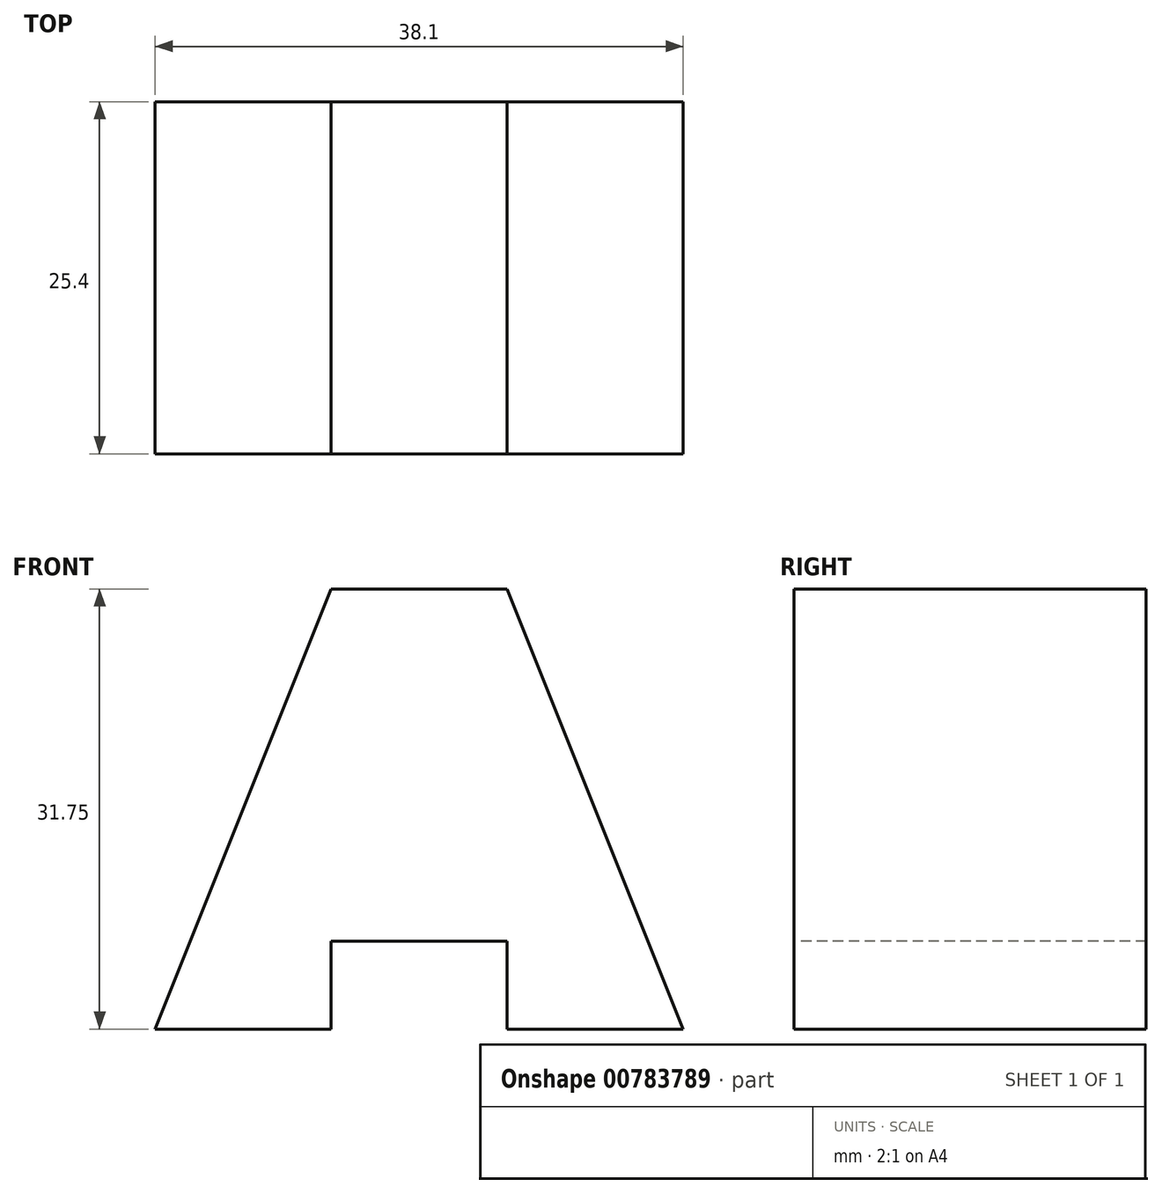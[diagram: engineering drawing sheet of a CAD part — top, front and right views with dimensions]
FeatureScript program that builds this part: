
annotation { "Feature Type Name" : "Feature", "Feature Type Description" : "" }
export const myFeature = defineFeature(function(context is Context, id is Id, definition is map)
    precondition{}
    {
        {
            var Q0;
            Q0=qCreatedBy(makeId("Front.planeOp"),FACE);
            var sketch = newSketch(context, id + "F0", { "sketchPlane" : qUnion([Q0])});
            skLineSegment(sketch, "E0", {"start": v(0, 0) * mm, "end": v(38.1, 0) * mm});
            skLineSegment(sketch, "E1", {"start": v(38.1, 0) * mm, "end": v(38.1, 31.75) * mm});
            skLineSegment(sketch, "E2", {"start": v(38.1, 31.75) * mm, "end": v(0, 31.75) * mm});
            skLineSegment(sketch, "E3", {"start": v(0, 31.75) * mm, "end": v(0, 0) * mm});
            skSolve(sketch);
        }
        {
            var Q0;
            Q0=makeQuery(id+"F0.imprint","IMPRINT",FACE,{"disambiguationData":[TD([[makeQuery(id+"F0.imprint","IMPRINT",EDGE,{"derivedFrom":sQuery(id+"F0.wireOp",EDGE,"E0")}),1.0]])]});
            extrude(context, id + "F1", {"entities" : qUnion([Q0]), "depth" : 25.4 * mm, "offsetDistance" : 25.4 * mm});
        }
        {
            var Q0;
            Q0=makeQuery(id+"F1.opExtrude","CAP_FACE",FACE,{"disambiguationData":[OSD([sQuery(id+"F0.wireOp",EDGE,"E0"),sQuery(id+"F0.wireOp",EDGE,"E1"),sQuery(id+"F0.wireOp",EDGE,"E2"),sQuery(id+"F0.wireOp",EDGE,"E3")])],"isStart":false});
            var sketch = newSketch(context, id + "F2", { "sketchPlane" : qUnion([Q0])});
            skLineSegment(sketch, "E4", {"start": v(0, 0) * mm, "end": v(12.7, 0) * mm});
            skLineSegment(sketch, "E5", {"start": v(12.7, 0) * mm, "end": v(12.7, 6.35) * mm});
            skLineSegment(sketch, "E6", {"start": v(12.7, 6.35) * mm, "end": v(25.4, 6.35) * mm});
            skLineSegment(sketch, "E7", {"start": v(25.4, 6.35) * mm, "end": v(25.4, 0) * mm});
            skLineSegment(sketch, "E8", {"start": v(25.4, 0) * mm, "end": v(38.1, 0) * mm});
            skSolve(sketch);
        }
        {
            var Q0;
            Q0 = qSketchRegion(id + "F2", true);
            var Q1;
            {var subQ0=sQuery(id+"F2.wireOp",EDGE,"E5");Q1=makeQuery(id+"F2.imprint","IMPRINT",FACE,{"disambiguationData":[TD([[makeQuery(id+"F2.imprint","IMPRINT",EDGE,{"derivedFrom":subQ0}),-1.0]])]});}
            extrude(context, id + "F3", {"entities" : qUnion([Q0, Q1]), "operationType" : NewBodyOperationType.REMOVE, "oppositeDirection" : true, "depth" : 25.4 * mm, "offsetDistance" : 25.4 * mm});
        }
        {
            var Q0;
            Q0=makeQuery(id+"F1.opExtrude","CAP_FACE",FACE,{"disambiguationData":[OSD([sQuery(id+"F0.wireOp",EDGE,"E0"),sQuery(id+"F0.wireOp",EDGE,"E1"),sQuery(id+"F0.wireOp",EDGE,"E2"),sQuery(id+"F0.wireOp",EDGE,"E3")])],"isStart":false});
            var sketch = newSketch(context, id + "F4", { "sketchPlane" : qUnion([Q0])});
            skLineSegment(sketch, "E9", {"start": v(0, 31.75) * mm, "end": v(12.7, 31.75) * mm});
            skLineSegment(sketch, "E10", {"start": v(12.7, 31.75) * mm, "end": v(25.4, 31.75) * mm});
            skLineSegment(sketch, "E11", {"start": v(25.4, 31.75) * mm, "end": v(38.1, 31.75) * mm});
            skLineSegment(sketch, "E12", {"start": v(0, 0) * mm, "end": v(12.7, 31.75) * mm});
            skLineSegment(sketch, "E13", {"start": v(25.4, 31.75) * mm, "end": v(38.1, 0) * mm});
            skSolve(sketch);
        }
        {
            var Q0;
            Q0 = qSketchRegion(id + "F4", true);
            var Q1;
            Q1=makeQuery(id+"F4.imprint","IMPRINT",FACE,{"disambiguationData":[TD([[makeQuery(id+"F4.imprint","IMPRINT",EDGE,{"derivedFrom":sQuery(id+"F4.wireOp",EDGE,"E9")}),1.0]])]});
            extrude(context, id + "F5", {"entities" : qUnion([Q0, Q1]), "operationType" : NewBodyOperationType.REMOVE, "oppositeDirection" : true, "depth" : 25.4 * mm, "offsetDistance" : 25.4 * mm});
        }
        {
            var Q0;
            Q0=makeQuery(id+"F1.opExtrude","CAP_FACE",FACE,{"disambiguationData":[OSD([sQuery(id+"F0.wireOp",EDGE,"E0"),sQuery(id+"F0.wireOp",EDGE,"E1"),sQuery(id+"F0.wireOp",EDGE,"E2"),sQuery(id+"F0.wireOp",EDGE,"E3")])],"isStart":false});
            var sketch = newSketch(context, id + "F6", { "sketchPlane" : qUnion([Q0])});
            skLineSegment(sketch, "E14", {"start": v(12.7, 31.75) * mm, "end": v(25.4, 31.75) * mm});
            skLineSegment(sketch, "E15", {"start": v(25.4, 31.75) * mm, "end": v(38.1, 0) * mm});
            skSolve(sketch);
        }
        {
            var Q0;
            Q0 = qSketchRegion(id + "F6", true);
            var Q1;
            {var subQ0=sQuery(id+"F6.wireOp",EDGE,"E15");Q1=makeQuery(id+"F6.imprint","IMPRINT",FACE,{"disambiguationData":[TD([[makeQuery(id+"F6.imprint","IMPRINT",EDGE,{"derivedFrom":subQ0}),1.0]])]});}
            extrude(context, id + "F7", {"entities" : qUnion([Q0, Q1]), "operationType" : NewBodyOperationType.REMOVE, "oppositeDirection" : true, "depth" : 25.4 * mm, "offsetDistance" : 25.4 * mm});
        }
    });
